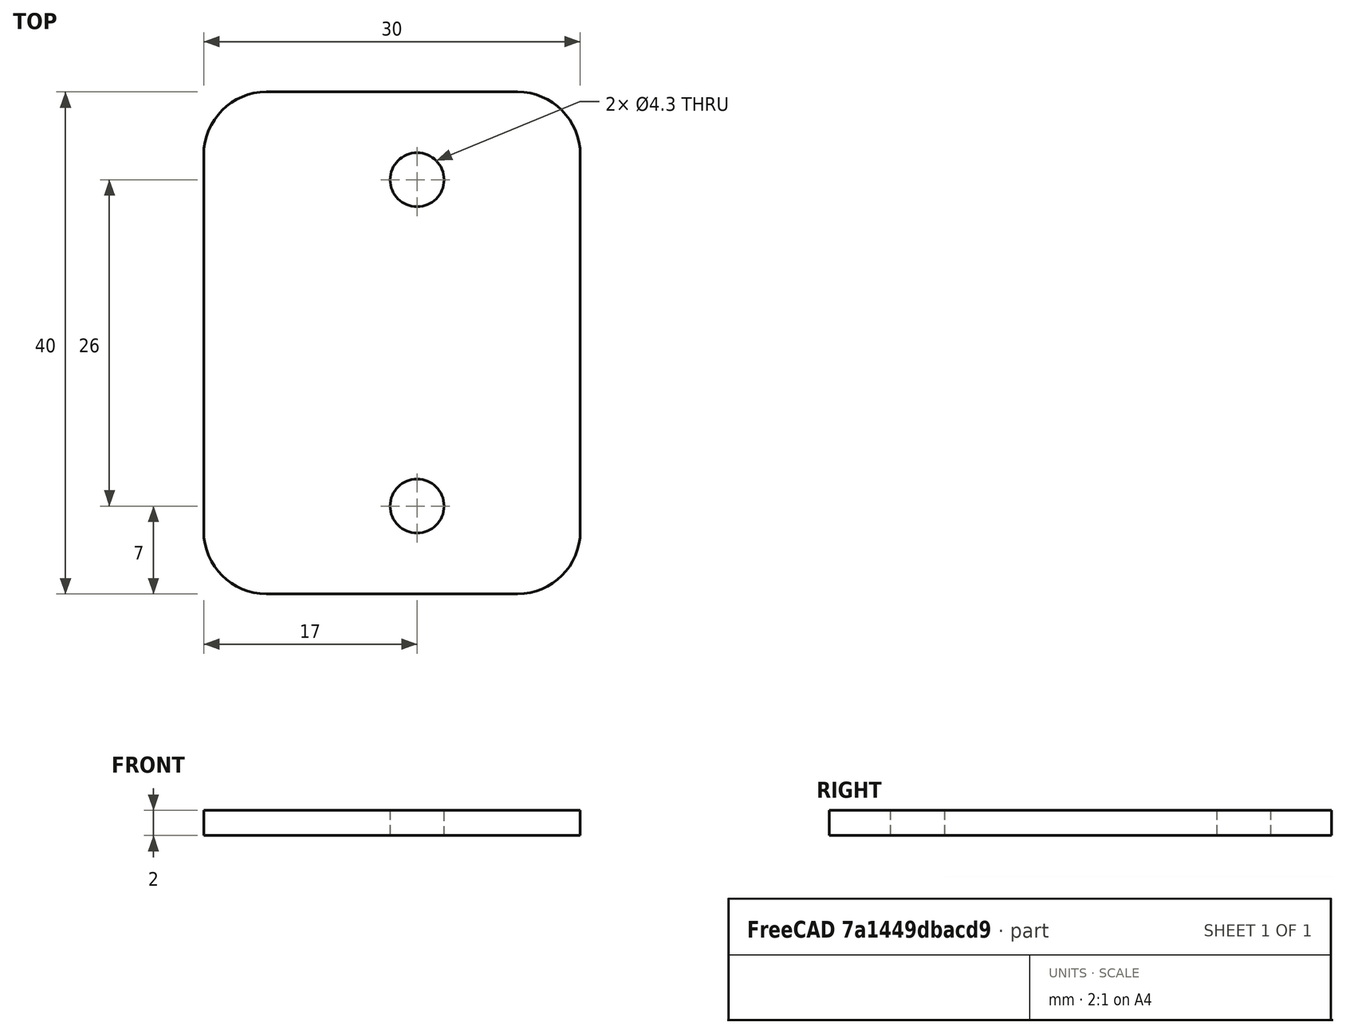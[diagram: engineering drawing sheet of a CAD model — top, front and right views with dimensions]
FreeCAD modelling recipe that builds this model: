
FCSTD DOCUMENT  (FreeCAD 1.0R39109 (Git))
Label: joint_plates_m4
License: All rights reserved
LicenseURL: https://en.wikipedia.org/wiki/All_rights_reserved
objects: Sketcher::SketchObject×1, PartDesign::Pad×1, PartDesign::Body×1
note: 6 computed .brp shape members not serialized (recipe doc carries the construction recipe); baked Part::Feature solids carry a one-line shape summary decoded from their .brp

FEATURE [Sketcher::SketchObject] Sketch
  ArcFitTolerance = 1e-06
  AttachmentSupport = -> [XY_Plane]
  FullyConstrained = true
  MakeInternals = false
  MapMode = 5
  sketch-geometry (12):
    g0: LineSegment StartX=-15 StartY=15 StartZ=0 EndX=-15 EndY=-15 EndZ=0
    g1: LineSegment StartX=-10 StartY=-20 StartZ=0 EndX=10 EndY=-20 EndZ=0
    g2: LineSegment StartX=15 StartY=-15 StartZ=0 EndX=15 EndY=15 EndZ=0
    g3: LineSegment StartX=10 StartY=20 StartZ=0 EndX=-10 EndY=20 EndZ=0
    g4: ArcOfCircle CenterX=-10 CenterY=15 CenterZ=0 NormalX=0 NormalY=0 NormalZ=1 AngleXU=0 Radius=5 StartAngle=1.5708 EndAngle=3.14159
    g5: ArcOfCircle CenterX=-10 CenterY=-15 CenterZ=0 NormalX=0 NormalY=0 NormalZ=1 AngleXU=0 Radius=5 StartAngle=3.14159 EndAngle=4.71239
    g6: ArcOfCircle CenterX=10 CenterY=-15 CenterZ=0 NormalX=0 NormalY=0 NormalZ=1 AngleXU=0 Radius=5 StartAngle=4.71239 EndAngle=6.28319
    g7: ArcOfCircle CenterX=10 CenterY=15 CenterZ=0 NormalX=0 NormalY=0 NormalZ=1 AngleXU=0 Radius=5 StartAngle=0 EndAngle=1.5708
    g8: GeomPoint [constr] X=-15 Y=20 Z=0
    g9: GeomPoint [constr] X=15 Y=-20 Z=0
    g10: Circle CenterX=2 CenterY=13 CenterZ=0 NormalX=0 NormalY=0 NormalZ=1 AngleXU=0 Radius=2.15
    g11: Circle CenterX=2 CenterY=-13 CenterZ=0 NormalX=0 NormalY=0 NormalZ=1 AngleXU=0 Radius=2.15
  constraints (28):
    c: Tangent(g0,g4) = -1.5708
    c: Tangent(g0,g5) = -1.5708
    c: Tangent(g1,g5) = -1.5708
    c: Tangent(g1,g6) = -1.5708
    c: Tangent(g2,g6) = -1.5708
    c: Tangent(g2,g7) = -1.5708
    c: Tangent(g3,g7) = -1.5708
    c: Tangent(g3,g4) = -1.5708
    c: Vertical(g0)
    c: Vertical(g2)
    c: Horizontal(g1)
    c: Horizontal(g3)
    c: Equal(g4,g5)
    c: Equal(g5,g6)
    c: Equal(g6,g7)
    c: PointOnObject(g8,g0)
    c: PointOnObject(g8,g3)
    c: PointOnObject(g9,g1)
    c: PointOnObject(g9,g2)
    c: Symmetric(g9,g8,g-1)
    c: DistanceY(g1,g3) = 40
    c: DistanceX(g0,g2) = 30
    c: DistanceY(g11,g10) = 26
    c: Symmetric(g11,g10,g-1)
    c: Radius(g11) = 2.15
    c: Equal(g11,g10)
    c: DistanceX(g11,g2) = 13
    c: Radius(g6) = 5
FEATURE [PartDesign::Pad] Pad  label="JointPad"
  Direction = (0,0,1)
  Length = 2
  Length2 = 10
  Profile = -> Sketch
  ReferenceAxis = -> Sketch [N_Axis]
  Refine = true
  Suppressed = false
  Type = 0
FEATURE [PartDesign::Body] Body  label="joint_plates_m4"
  AllowCompound = false
  Group = -> [Sketch,Pad]
  Origin = -> Origin
  Tip = -> Pad
